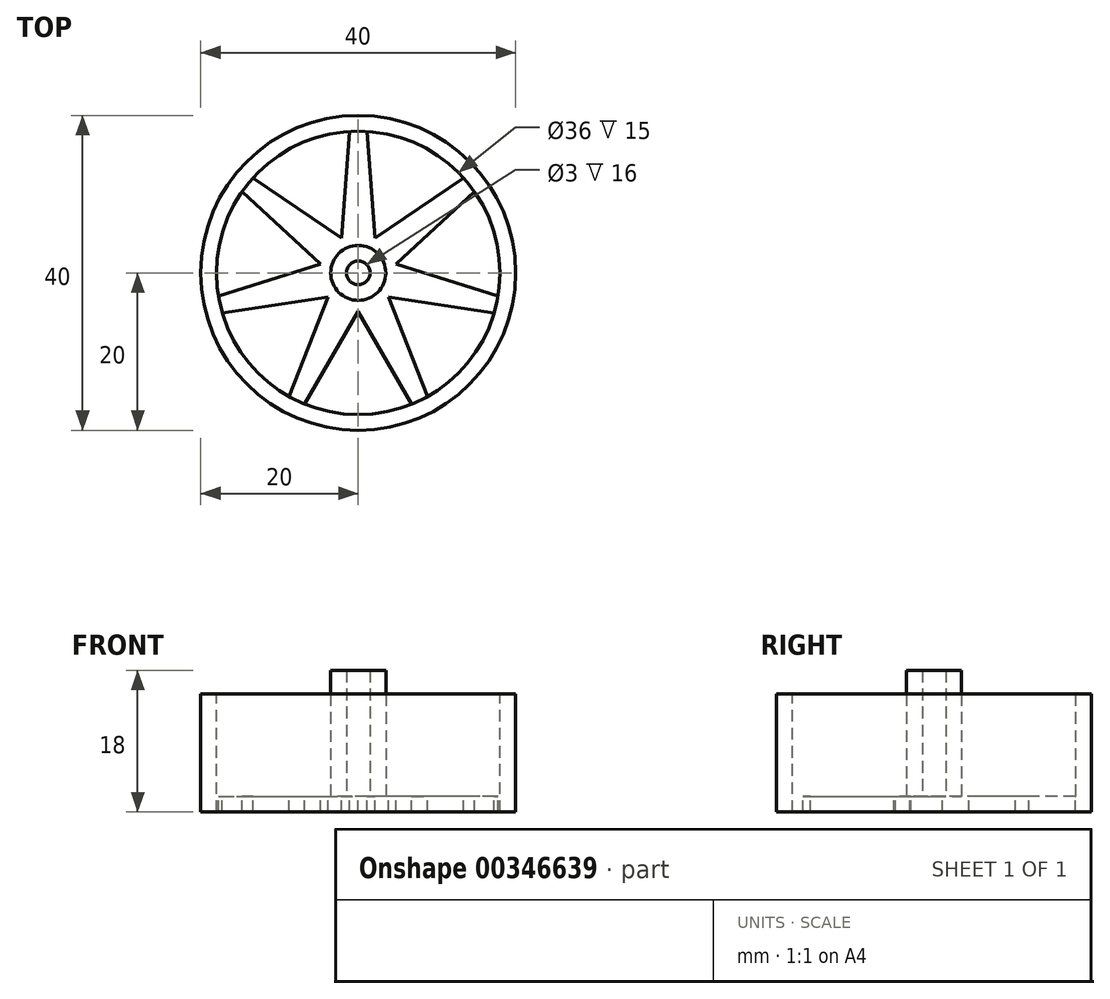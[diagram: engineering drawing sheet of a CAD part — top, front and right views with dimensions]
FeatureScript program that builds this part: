
annotation { "Feature Type Name" : "Feature", "Feature Type Description" : "" }
export const myFeature = defineFeature(function(context is Context, id is Id, definition is map)
    precondition{}
    {
        {
            var Q0;
            Q0=qCreatedBy(makeId("Top.planeOp"),FACE);
            var sketch = newSketch(context, id + "F0", { "sketchPlane" : qUnion([Q0])});
            skCircle(sketch, "E0", {"center": v(0, 0) * mm, "radius": 20 * mm});
            skSolve(sketch);
        }
        {
            var Q0;
            Q0=makeQuery(id+"F0.imprint","IMPRINT",FACE,{"disambiguationData":[TD([[makeQuery(id+"F0.imprint","IMPRINT",EDGE,{"derivedFrom":sQuery(id+"F0.wireOp",EDGE,"E0")}),1.0]])]});
            extrude(context, id + "F1", {"entities" : qUnion([Q0]), "depth" : 15 * mm});
        }
        {
            var Q0;
            Q0=makeQuery(id+"F1.opExtrude","CAP_FACE",FACE,{"disambiguationData":[OSD([sQuery(id+"F0.wireOp",EDGE,"E0")])],"isStart":false});
            var sketch = newSketch(context, id + "F2", { "sketchPlane" : qUnion([Q0])});
            skCircle(sketch, "E1", {"center": v(0, 0) * mm, "radius": 18 * mm});
            skSolve(sketch);
        }
        {
            var Q0;
            Q0=makeQuery(id+"F2.imprint","IMPRINT",FACE,{"disambiguationData":[TD([[makeQuery(id+"F2.imprint","IMPRINT",EDGE,{"derivedFrom":sQuery(id+"F2.wireOp",EDGE,"E1")}),1.0]])]});
            extrude(context, id + "F3", {"entities" : qUnion([Q0]), "operationType" : NewBodyOperationType.REMOVE, "oppositeDirection" : true, "depth" : 13 * mm});
        }
        {
            var Q0;
            Q0=makeQuery(id+"F3.boolean.opBoolean","COPY",FACE,{"derivedFrom":makeQuery(id+"F3.opExtrude","CAP_FACE",FACE,{"disambiguationData":[OSD([sQuery(id+"F2.wireOp",EDGE,"E1")])],"isStart":false})});
            var sketch = newSketch(context, id + "F4", { "sketchPlane" : qUnion([Q0])});
            skSolve(sketch);
        }
        {
            var Q0;
            Q0=makeQuery(id+"F4.imprint","IMPRINT",FACE,{"disambiguationData":[TD([[makeQuery(id+"F4.imprint","IMPRINT",EDGE,{"derivedFrom":makeQuery(id+"F3.boolean.opBoolean","COPY",EDGE,{"derivedFrom":makeQuery(id+"F3.opExtrude","CAP_EDGE",EDGE,{"disambiguationData":[OSD([sQuery(id+"F2.wireOp",EDGE,"E1")])],"isStart":false})})}),1.0]])]});
            var sketch = newSketch(context, id + "F5", { "sketchPlane" : qUnion([Q0])});
            skCircle(sketch, "E2", {"center": v(0, 0) * mm, "radius": 3.5 * mm});
            skCircle(sketch, "E3", {"center": v(0, 0) * mm, "radius": 1.5 * mm});
            skSolve(sketch);
        }
        {
            var Q0;
            Q0 = qSketchRegion(id + "F5", true);
            extrude(context, id + "F6", {"entities" : qUnion([Q0]), "operationType" : NewBodyOperationType.ADD, "depth" : 16 * mm});
        }
        {
            var Q0;
            Q0=makeQuery(id+"F4.imprint","IMPRINT",FACE,{"disambiguationData":[TD([[makeQuery(id+"F4.imprint","IMPRINT",EDGE,{"derivedFrom":makeQuery(id+"F3.boolean.opBoolean","COPY",EDGE,{"derivedFrom":makeQuery(id+"F3.opExtrude","CAP_EDGE",EDGE,{"disambiguationData":[OSD([sQuery(id+"F2.wireOp",EDGE,"E1")])],"isStart":false})})}),1.0]])]});
            var sketch = newSketch(context, id + "F7", { "sketchPlane" : qUnion([Q0])});
            skLineSegment(sketch, "E4", {"start": v(-1.1, 18.07) * mm, "end": v(-2.3, 2.18) * mm});
            skLineSegment(sketch, "E5.MirrorCS", {"start": v(1.1, 18.07) * mm, "end": v(2.3, 2.18) * mm});
            skLineSegment(sketch, "E6.1.0", {"start": v(-13.44, 12.13) * mm, "end": v(-0.27, 3.16) * mm});
            skLineSegment(sketch, "E6.1.1", {"start": v(-14.82, 10.4) * mm, "end": v(-3.14, -0.44) * mm});
            skLineSegment(sketch, "E6.2.0", {"start": v(-17.87, -2.94) * mm, "end": v(-2.64, 1.76) * mm});
            skLineSegment(sketch, "E6.2.1", {"start": v(-17.37, -5.1) * mm, "end": v(-1.62, -2.73) * mm});
            skLineSegment(sketch, "E6.3.0", {"start": v(-8.84, -15.8) * mm, "end": v(-3.02, -0.97) * mm});
            skLineSegment(sketch, "E6.3.1", {"start": v(-6.85, -16.76) * mm, "end": v(1.13, -2.97) * mm});
            skLineSegment(sketch, "E6.4.0", {"start": v(6.85, -16.76) * mm, "end": v(-1.13, -2.97) * mm});
            skLineSegment(sketch, "E6.4.1", {"start": v(8.84, -15.8) * mm, "end": v(3.02, -0.97) * mm});
            skLineSegment(sketch, "E6.5.0", {"start": v(17.37, -5.1) * mm, "end": v(1.62, -2.73) * mm});
            skLineSegment(sketch, "E6.5.1", {"start": v(17.87, -2.94) * mm, "end": v(2.64, 1.76) * mm});
            skLineSegment(sketch, "E6.6.0", {"start": v(14.82, 10.4) * mm, "end": v(3.14, -0.44) * mm});
            skLineSegment(sketch, "E6.6.1", {"start": v(13.44, 12.13) * mm, "end": v(0.27, 3.16) * mm});
            skPoint(sketch, "E6.center", {"position": v(0, 0) * mm});
            skCircle(sketch, "E7", {"center": v(0, 0) * mm, "radius": 18 * mm});
            skSolve(sketch);
        }
        {
            var Q0;
            {var subQ0=sQuery(id+"F7.wireOp",EDGE,"E6.3.0");var subQ1=sQuery(id+"F7.wireOp",EDGE,"E6.2.1");var subQ2=makeQuery(id+"F7.imprint","INTERSECT",VERTEX,{"derivedFrom":[subQ1,subQ0]});Q0=makeQuery(id+"F7.imprint","IMPRINT",FACE,{"disambiguationData":[TD([[makeQuery(id+"F7.imprint","IMPRINT",EDGE,{"disambiguationData":[TD([[subQ2,1.0]])],"derivedFrom":subQ1}),-1.0]])]});}
            var Q1;
            {var subQ0=sQuery(id+"F7.wireOp",EDGE,"E6.4.0");var subQ1=sQuery(id+"F7.wireOp",EDGE,"E6.3.1");var subQ2=makeQuery(id+"F7.imprint","INTERSECT",VERTEX,{"derivedFrom":[subQ1,subQ0]});Q1=makeQuery(id+"F7.imprint","IMPRINT",FACE,{"disambiguationData":[TD([[makeQuery(id+"F7.imprint","IMPRINT",EDGE,{"disambiguationData":[TD([[subQ2,1.0]])],"derivedFrom":subQ1}),-1.0]])]});}
            var Q2;
            {var subQ0=sQuery(id+"F7.wireOp",EDGE,"E6.2.0");var subQ1=sQuery(id+"F7.wireOp",EDGE,"E6.1.1");var subQ2=makeQuery(id+"F7.imprint","INTERSECT",VERTEX,{"derivedFrom":[subQ1,subQ0]});Q2=makeQuery(id+"F7.imprint","IMPRINT",FACE,{"disambiguationData":[TD([[makeQuery(id+"F7.imprint","IMPRINT",EDGE,{"disambiguationData":[TD([[subQ2,1.0]])],"derivedFrom":subQ1}),-1.0]])]});}
            var Q3;
            {var subQ0=sQuery(id+"F7.wireOp",EDGE,"E6.1.0");var subQ1=sQuery(id+"F7.wireOp",EDGE,"E4");var subQ2=makeQuery(id+"F7.imprint","INTERSECT",VERTEX,{"derivedFrom":[subQ1,subQ0]});Q3=makeQuery(id+"F7.imprint","IMPRINT",FACE,{"disambiguationData":[TD([[makeQuery(id+"F7.imprint","IMPRINT",EDGE,{"disambiguationData":[TD([[subQ2,1.0]])],"derivedFrom":subQ1}),-1.0]])]});}
            var Q4;
            {var subQ0=sQuery(id+"F7.wireOp",EDGE,"E6.6.1");var subQ1=sQuery(id+"F7.wireOp",EDGE,"E5.MirrorCS");var subQ2=makeQuery(id+"F7.imprint","INTERSECT",VERTEX,{"derivedFrom":[subQ1,subQ0]});Q4=makeQuery(id+"F7.imprint","IMPRINT",FACE,{"disambiguationData":[TD([[makeQuery(id+"F7.imprint","IMPRINT",EDGE,{"disambiguationData":[TD([[subQ2,1.0]])],"derivedFrom":subQ1}),1.0]])]});}
            var Q5;
            {var subQ0=sQuery(id+"F7.wireOp",EDGE,"E6.6.0");var subQ1=sQuery(id+"F7.wireOp",EDGE,"E6.5.1");var subQ2=makeQuery(id+"F7.imprint","INTERSECT",VERTEX,{"derivedFrom":[subQ1,subQ0]});Q5=makeQuery(id+"F7.imprint","IMPRINT",FACE,{"disambiguationData":[TD([[makeQuery(id+"F7.imprint","IMPRINT",EDGE,{"disambiguationData":[TD([[subQ2,1.0]])],"derivedFrom":subQ1}),-1.0]])]});}
            var Q6;
            {var subQ0=sQuery(id+"F7.wireOp",EDGE,"E6.5.0");var subQ1=sQuery(id+"F7.wireOp",EDGE,"E6.4.1");var subQ2=makeQuery(id+"F7.imprint","INTERSECT",VERTEX,{"derivedFrom":[subQ1,subQ0]});Q6=makeQuery(id+"F7.imprint","IMPRINT",FACE,{"disambiguationData":[TD([[makeQuery(id+"F7.imprint","IMPRINT",EDGE,{"disambiguationData":[TD([[subQ2,1.0]])],"derivedFrom":subQ1}),-1.0]])]});}
            extrude(context, id + "F8", {"entities" : qUnion([Q0, Q1, Q2, Q3, Q4, Q5, Q6]), "operationType" : NewBodyOperationType.REMOVE, "oppositeDirection" : true, "depth" : 2 * mm});
        }
    });
